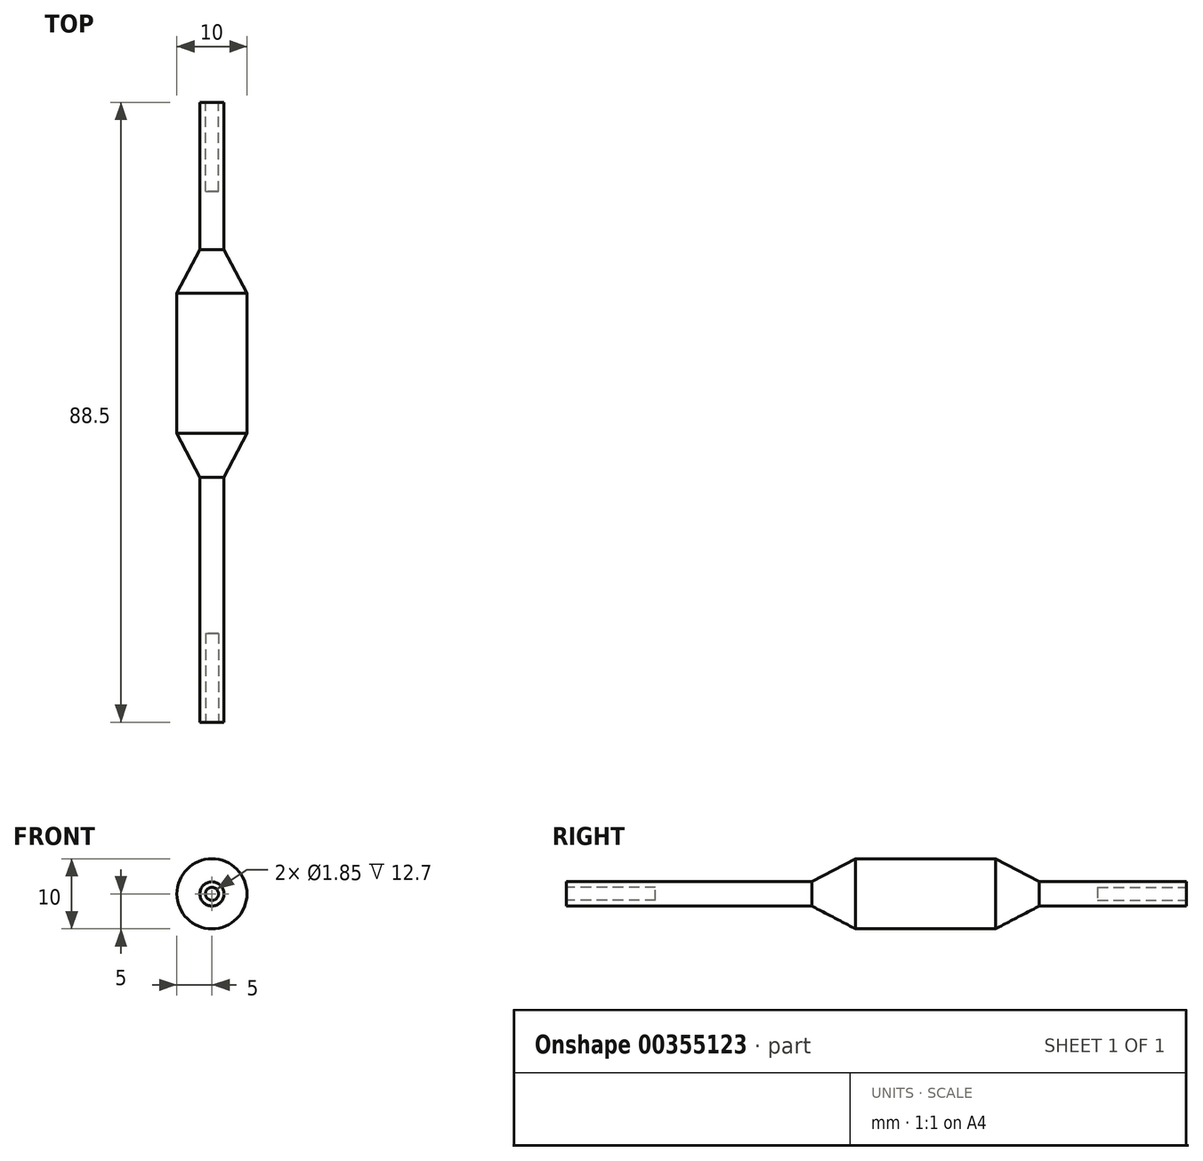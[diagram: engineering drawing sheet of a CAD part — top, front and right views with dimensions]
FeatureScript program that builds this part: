
annotation { "Feature Type Name" : "Feature", "Feature Type Description" : "" }
export const myFeature = defineFeature(function(context is Context, id is Id, definition is map)
    precondition{}
    {
        {
            var Q0;
            Q0=qCreatedBy(makeId("Right.planeOp"),FACE);
            var sketch = newSketch(context, id + "F0", { "sketchPlane" : qUnion([Q0])});
            skLineSegment(sketch, "E0", {"start": v(0, 0) * mm, "end": v(0, 1.73) * mm});
            skLineSegment(sketch, "E1", {"start": v(0, 1.73) * mm, "end": v(35, 1.73) * mm});
            skLineSegment(sketch, "E2", {"start": v(35, 1.73) * mm, "end": v(41.25, 5) * mm});
            skLineSegment(sketch, "E3", {"start": v(41.25, 5) * mm, "end": v(61.25, 5) * mm});
            skLineSegment(sketch, "E4", {"start": v(61.25, 5) * mm, "end": v(67.5, 1.73) * mm});
            skLineSegment(sketch, "E5", {"start": v(67.5, 1.73) * mm, "end": v(88.5, 1.73) * mm});
            skLineSegment(sketch, "E6", {"start": v(88.5, 1.73) * mm, "end": v(88.5, 0) * mm});
            skLineSegment(sketch, "E7", {"start": v(0, 0) * mm, "end": v(88.5, 0) * mm, "construction": true});
            skLineSegment(sketch, "E8", {"start": v(51.25, 5) * mm, "end": v(51.25, 0) * mm, "construction": true});
            skLineSegment(sketch, "E9", {"start": v(0, 0) * mm, "end": v(88.5, 0) * mm});
            skSolve(sketch);
        }
        {
            var Q0;
            Q0 = qSketchRegion(id + "F0", true);
            var Q1;
            Q1=sQuery(id+"F0.wireOp",EDGE,"E7");
            revolve(context, id + "F1", {"entities" : qUnion([Q0]), "axis" : qUnion([Q1]), "revolveType" : RevolveType.FULL});
        }
        {
            var Q0;
            Q0=makeQuery(id+"F1.opRevolve","SWEPT_FACE",FACE,{"disambiguationData":[OSD([sQuery(id+"F0.wireOp",EDGE,"E0")])]});
            var sketch = newSketch(context, id + "F2", { "sketchPlane" : qUnion([Q0])});
            skCircle(sketch, "E10", {"center": v(0, 0) * mm, "radius": 0.93 * mm});
            skSolve(sketch);
        }
        {
            var Q0;
            Q0 = qSketchRegion(id + "F2", true);
            extrude(context, id + "F3", {"entities" : qUnion([Q0]), "operationType" : NewBodyOperationType.REMOVE, "oppositeDirection" : true, "depth" : 12.7 * mm});
        }
        {
            var Q0;
            Q0=makeQuery(id+"F1.opRevolve","SWEPT_FACE",FACE,{"disambiguationData":[OSD([sQuery(id+"F0.wireOp",EDGE,"E6")])]});
            var sketch = newSketch(context, id + "F4", { "sketchPlane" : qUnion([Q0])});
            skCircle(sketch, "E11", {"center": v(0, 0) * mm, "radius": 0.93 * mm});
            skSolve(sketch);
        }
        {
            var Q0;
            Q0 = qSketchRegion(id + "F4", true);
            extrude(context, id + "F5", {"entities" : qUnion([Q0]), "operationType" : NewBodyOperationType.REMOVE, "oppositeDirection" : true, "depth" : 12.7 * mm});
        }
    });
